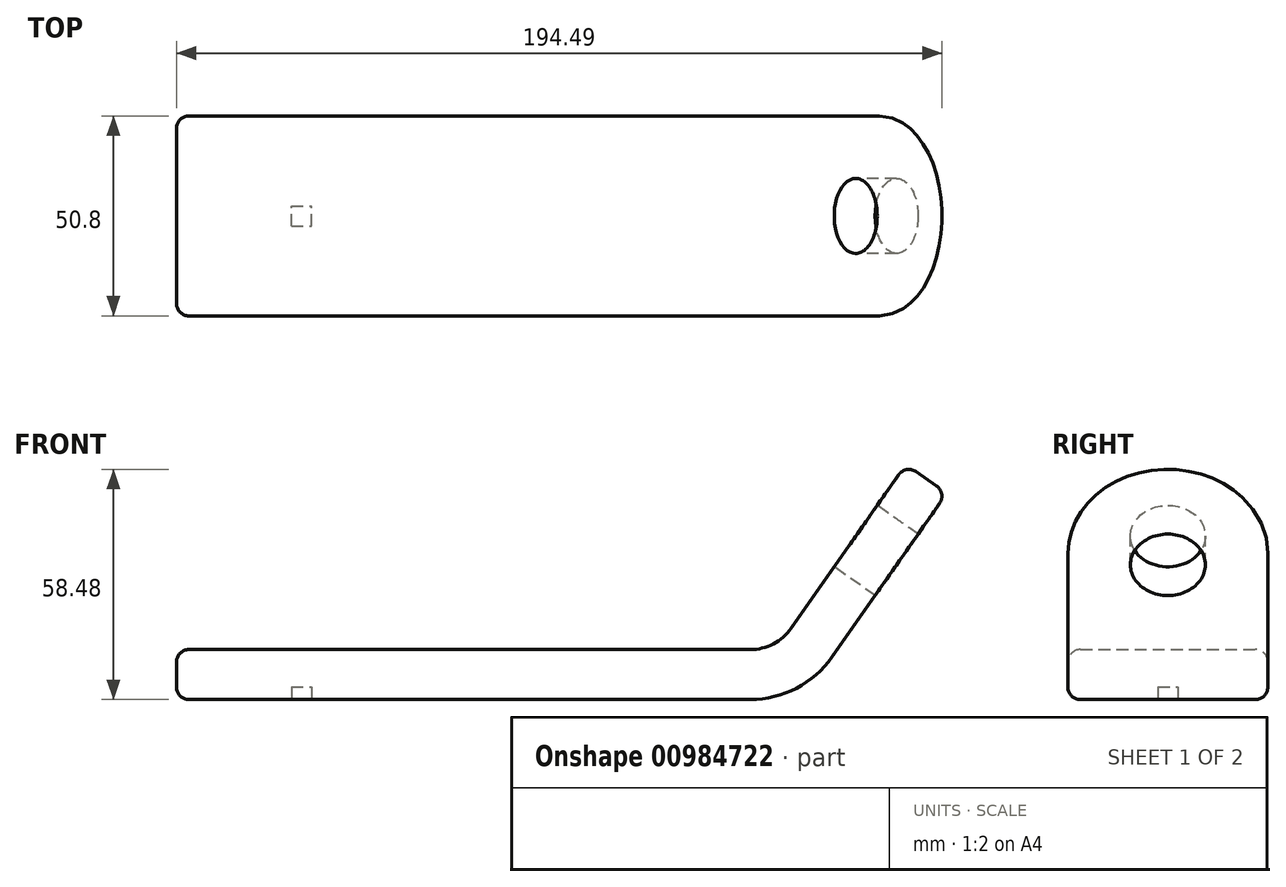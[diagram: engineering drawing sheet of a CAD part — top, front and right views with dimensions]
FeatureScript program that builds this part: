
annotation { "Feature Type Name" : "Feature", "Feature Type Description" : "" }
export const myFeature = defineFeature(function(context is Context, id is Id, definition is map)
    precondition{}
    {
        {
            var Q0;
            Q0=qCreatedBy(makeId("Front.planeOp"),FACE);
            var sketch = newSketch(context, id + "F0", { "sketchPlane" : qUnion([Q0])});
            skLineSegment(sketch, "E0", {"start": v(-26.8, 10.63) * mm, "end": v(118.99, 10.63) * mm});
            skLineSegment(sketch, "E1", {"start": v(129.4, 16.05) * mm, "end": v(158.53, 57.66) * mm});
            skLineSegment(sketch, "E2", {"start": v(158.53, 57.66) * mm, "end": v(168.93, 50.38) * mm});
            skLineSegment(sketch, "E3", {"start": v(168.93, 50.38) * mm, "end": v(139.8, 8.76) * mm});
            skLineSegment(sketch, "E4", {"start": v(118.99, -2.07) * mm, "end": v(-26.8, -2.07) * mm});
            skLineSegment(sketch, "E5", {"start": v(-26.8, -2.07) * mm, "end": v(-26.8, 10.63) * mm});
            skPoint(sketch, "E6.visualSharp", {"position": v(125.6, 10.63) * mm});
            skArc(sketch, "E6.filletArc", {"start": v(118.99, 10.63) * mm, "mid": v(124.85, 12.07) * mm, "end": v(129.4, 16.05) * mm});
            skPoint(sketch, "E7.visualSharp", {"position": v(132.21, -2.07) * mm});
            skArc(sketch, "E7.filletArc", {"start": v(118.99, -2.07) * mm, "mid": v(130.72, 0.8) * mm, "end": v(139.8, 8.76) * mm});
            skSolve(sketch);
        }
        {
            var Q0;
            Q0=makeQuery(id+"F0.imprint","IMPRINT",FACE,{"disambiguationData":[TD([[makeQuery(id+"F0.imprint","IMPRINT",EDGE,{"derivedFrom":sQuery(id+"F0.wireOp",EDGE,"E0")}),-1.0]])]});
            extrude(context, id + "F1", {"entities" : qUnion([Q0]), "depth" : 50.8 * mm, "offsetDistance" : 25.4 * mm, "symmetric" : true});
        }
        {
            var Q0;
            Q0=makeQuery(id+"F1.opExtrude","SWEPT_FACE",FACE,{"disambiguationData":[OSD([sQuery(id+"F0.wireOp",EDGE,"E1")])]});
            var sketch = newSketch(context, id + "F2", { "sketchPlane" : qUnion([Q0])});
            skCircle(sketch, "E8", {"center": v(0, 115.94) * mm, "radius": 9.53 * mm});
            skSolve(sketch);
        }
        {
            var Q0;
            Q0=makeQuery(id+"F2.imprint","IMPRINT",FACE,{"disambiguationData":[TD([[makeQuery(id+"F2.imprint","IMPRINT",EDGE,{"derivedFrom":sQuery(id+"F2.wireOp",EDGE,"E8")}),1.0]])]});
            extrude(context, id + "F3", {"entities" : qUnion([Q0]), "operationType" : NewBodyOperationType.REMOVE, "endBound" : BoundingType.THROUGH_ALL, "oppositeDirection" : true, "depth" : 25.4 * mm, "offsetDistance" : 25.4 * mm});
        }
        {
            var Q0;
            Q0=makeQuery(id+"F1.opExtrude","CAP_EDGE",EDGE,{"disambiguationData":[OSD([sQuery(id+"F0.wireOp",EDGE,"E2")])],"isStart":true});
            var Q1;
            Q1=makeQuery(id+"F1.opExtrude","CAP_EDGE",EDGE,{"disambiguationData":[OSD([sQuery(id+"F0.wireOp",EDGE,"E2")])],"isStart":false});
            fillet(context, id + "F4", {"entities" : qUnion([Q0, Q1]), "radius" : 25.4 * mm, "tangentPropagation" : true, "allowEdgeOverflow" : false});
        }
        {
            var Q0;
            Q0=makeQuery(id+"F1.opExtrude","CAP_EDGE",EDGE,{"disambiguationData":[OSD([sQuery(id+"F0.wireOp",EDGE,"E5")])],"isStart":false});
            var Q1;
            Q1=makeQuery(id+"F1.opExtrude","CAP_EDGE",EDGE,{"disambiguationData":[OSD([sQuery(id+"F0.wireOp",EDGE,"E5")])],"isStart":true});
            fillet(context, id + "F5", {"entities" : qUnion([Q0, Q1]), "radius" : 3.17 * mm, "tangentPropagation" : true, "allowEdgeOverflow" : false});
        }
        {
            var Q0;
            Q0=makeQuery(id+"F1.opExtrude","SWEPT_FACE",FACE,{"disambiguationData":[OSD([sQuery(id+"F0.wireOp",EDGE,"E4")])]});
            var sketch = newSketch(context, id + "F6", { "sketchPlane" : qUnion([Q0])});
            skLineSegment(sketch, "E9.bottom", {"start": v(2.41, 2.54) * mm, "end": v(7.49, 2.54) * mm});
            skLineSegment(sketch, "E9.top", {"start": v(2.41, -2.54) * mm, "end": v(7.49, -2.54) * mm});
            skLineSegment(sketch, "E9.left", {"start": v(2.41, 2.54) * mm, "end": v(2.41, -2.54) * mm});
            skLineSegment(sketch, "E9.right", {"start": v(7.49, 2.54) * mm, "end": v(7.49, -2.54) * mm});
            skPoint(sketch, "E9.middle", {"position": v(4.95, 0) * mm});
            skSolve(sketch);
        }
        {
            var Q0;
            Q0=makeQuery(id+"F6.imprint","IMPRINT",FACE,{"disambiguationData":[TD([[makeQuery(id+"F6.imprint","IMPRINT",EDGE,{"derivedFrom":sQuery(id+"F6.wireOp",EDGE,"E9.bottom")}),-1.0]])]});
            extrude(context, id + "F7", {"entities" : qUnion([Q0]), "operationType" : NewBodyOperationType.REMOVE, "oppositeDirection" : true, "depth" : 3.17 * mm, "offsetDistance" : 25.4 * mm});
        }
        {
            var Q0;
            Q0=makeQuery(id+"F1.opExtrude","CAP_EDGE",EDGE,{"disambiguationData":[OSD([sQuery(id+"F0.wireOp",EDGE,"E0")])],"isStart":true});
            var Q1;
            Q1=makeQuery(id+"F1.opExtrude","CAP_EDGE",EDGE,{"disambiguationData":[OSD([sQuery(id+"F0.wireOp",EDGE,"E1")])],"isStart":true});
            var Q2;
            Q2=makeQuery(id+"F4.opFillet","BLEND_EDGE",EDGE,{"blendedFrom":[makeQuery(id+"F1.opExtrude","CAP_EDGE",EDGE,{"disambiguationData":[OSD([sQuery(id+"F0.wireOp",EDGE,"E2")])],"isStart":true}),makeQuery(id+"F1.opExtrude","SWEPT_FACE",FACE,{"disambiguationData":[OSD([sQuery(id+"F0.wireOp",EDGE,"E1")])]})],"blendedInto":[makeQuery(id+"F1.opExtrude","SWEPT_FACE",FACE,{"disambiguationData":[OSD([sQuery(id+"F0.wireOp",EDGE,"E1")])]})]});
            var Q3;
            Q3=makeQuery(id+"F1.opExtrude","CAP_EDGE",EDGE,{"disambiguationData":[OSD([sQuery(id+"F0.wireOp",EDGE,"E1")])],"isStart":false});
            var Q4;
            Q4=makeQuery(id+"F1.opExtrude","CAP_EDGE",EDGE,{"disambiguationData":[OSD([sQuery(id+"F0.wireOp",EDGE,"E0")])],"isStart":false});
            var Q5;
            Q5=makeQuery(id+"F1.opExtrude","SWEPT_EDGE",EDGE,{"disambiguationData":[OSD([sQuery(id+"F0.wireOp",EDGE,"E0"),sQuery(id+"F0.wireOp",EDGE,"E5")])]});
            var Q6;
            Q6=makeQuery(id+"F1.opExtrude","SWEPT_EDGE",EDGE,{"disambiguationData":[OSD([sQuery(id+"F0.wireOp",EDGE,"E4"),sQuery(id+"F0.wireOp",EDGE,"E5")])]});
            var Q7;
            Q7=makeQuery(id+"F1.opExtrude","CAP_EDGE",EDGE,{"disambiguationData":[OSD([sQuery(id+"F0.wireOp",EDGE,"E4")])],"isStart":false});
            fillet(context, id + "F8", {"entities" : qUnion([Q0, Q1, Q2, Q3, Q4, Q5, Q6, Q7]), "radius" : 3.17 * mm, "tangentPropagation" : true, "allowEdgeOverflow" : false});
        }
    });
